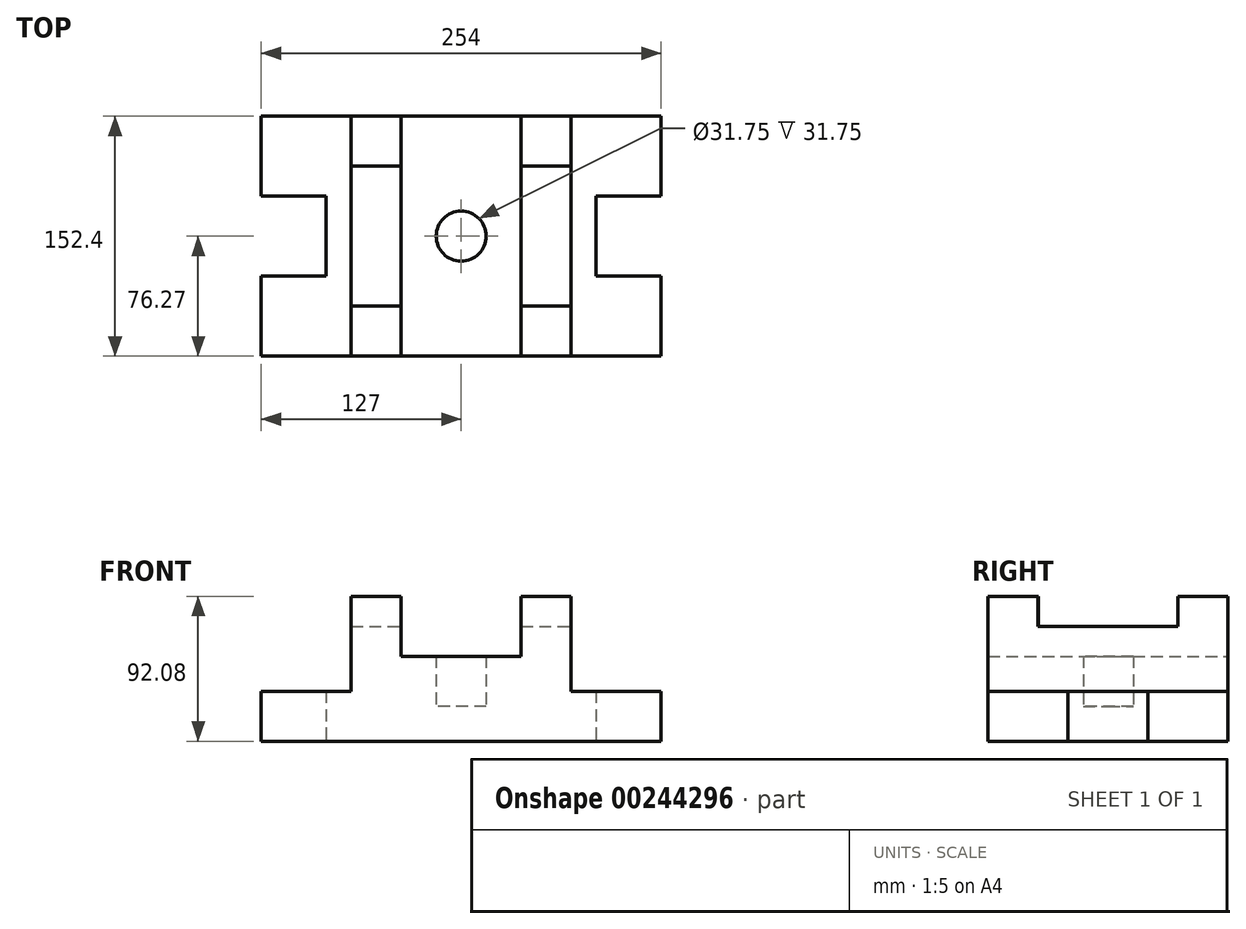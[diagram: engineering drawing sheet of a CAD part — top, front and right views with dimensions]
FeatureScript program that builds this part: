
annotation { "Feature Type Name" : "Feature", "Feature Type Description" : "" }
export const myFeature = defineFeature(function(context is Context, id is Id, definition is map)
    precondition{}
    {
        {
            var Q0;
            Q0=qCreatedBy(makeId("Top.planeOp"),FACE);
            var sketch = newSketch(context, id + "F0", { "sketchPlane" : qUnion([Q0])});
            skCircle(sketch, "E0", {"center": v(0, 0) * mm, "radius": 15.88 * mm});
            skLineSegment(sketch, "E1.bottom", {"start": v(-38.1, -76.27) * mm, "end": v(38.1, -76.27) * mm});
            skLineSegment(sketch, "E1.top", {"start": v(-38.1, 76.13) * mm, "end": v(38.1, 76.13) * mm});
            skLineSegment(sketch, "E1.left", {"start": v(-38.1, -76.27) * mm, "end": v(-38.1, 76.13) * mm});
            skLineSegment(sketch, "E1.right", {"start": v(38.1, -76.27) * mm, "end": v(38.1, 76.13) * mm});
            skLineSegment(sketch, "E2.bottom", {"start": v(38.1, 76.13) * mm, "end": v(69.85, 76.13) * mm});
            skLineSegment(sketch, "E2.top", {"start": v(38.1, 44.38) * mm, "end": v(69.85, 44.38) * mm});
            skLineSegment(sketch, "E2.left", {"start": v(38.1, 76.13) * mm, "end": v(38.1, 44.38) * mm});
            skLineSegment(sketch, "E2.right", {"start": v(69.85, 76.13) * mm, "end": v(69.85, 44.38) * mm});
            skLineSegment(sketch, "E3.bottom", {"start": v(38.1, -76.27) * mm, "end": v(69.85, -76.27) * mm});
            skLineSegment(sketch, "E3.top", {"start": v(38.1, -44.52) * mm, "end": v(69.85, -44.52) * mm});
            skLineSegment(sketch, "E3.left", {"start": v(38.1, -76.27) * mm, "end": v(38.1, -44.52) * mm});
            skLineSegment(sketch, "E3.right", {"start": v(69.85, -76.27) * mm, "end": v(69.85, -44.52) * mm});
            skLineSegment(sketch, "E4", {"start": v(69.85, 44.38) * mm, "end": v(69.85, -44.52) * mm});
            skLineSegment(sketch, "E5.MirrorCS", {"start": v(-38.1, -76.27) * mm, "end": v(-69.85, -76.27) * mm});
            skLineSegment(sketch, "E6.bottom", {"start": v(69.85, -76.27) * mm, "end": v(127, -76.27) * mm});
            skLineSegment(sketch, "E6.top", {"start": v(69.85, 76.13) * mm, "end": v(127, 76.13) * mm});
            skLineSegment(sketch, "E6.left", {"start": v(69.85, -76.27) * mm, "end": v(69.85, 76.13) * mm});
            skLineSegment(sketch, "E7.MirrorCS", {"start": v(-69.85, 76.13) * mm, "end": v(-127, 76.13) * mm});
            skLineSegment(sketch, "E8.MirrorCS", {"start": v(-127, -76.27) * mm, "end": v(-127, -25.47) * mm});
            skLineSegment(sketch, "E9.MirrorCS", {"start": v(-69.85, -76.27) * mm, "end": v(-127, -76.27) * mm});
            skLineSegment(sketch, "E10", {"start": v(127, -76.27) * mm, "end": v(127, -25.47) * mm});
            skLineSegment(sketch, "E11.bottom", {"start": v(127, 25.33) * mm, "end": v(85.73, 25.33) * mm});
            skLineSegment(sketch, "E11.top", {"start": v(127, -25.47) * mm, "end": v(85.73, -25.47) * mm});
            skLineSegment(sketch, "E11.right", {"start": v(85.73, 25.33) * mm, "end": v(85.73, -25.47) * mm});
            skLineSegment(sketch, "E12.trimOffspring", {"start": v(127, 25.33) * mm, "end": v(127, 76.13) * mm});
            skLineSegment(sketch, "E13.MirrorCS", {"start": v(-127, 25.33) * mm, "end": v(-85.73, 25.33) * mm});
            skLineSegment(sketch, "E14.MirrorCS", {"start": v(-85.73, 25.33) * mm, "end": v(-85.73, -25.47) * mm});
            skLineSegment(sketch, "E15.MirrorCS", {"start": v(-127, -25.47) * mm, "end": v(-85.73, -25.47) * mm});
            skLineSegment(sketch, "E16.trimOffspring", {"start": v(-127, 25.33) * mm, "end": v(-127, 76.13) * mm});
            skLineSegment(sketch, "E17.0", {"start": v(-38.21, 107.88) * mm, "end": v(-69.96, 107.88) * mm});
            skLineSegment(sketch, "E18", {"start": v(-69.85, 76.13) * mm, "end": v(-69.85, -76.27) * mm});
            skLineSegment(sketch, "E19.bottom", {"start": v(-69.85, 76.13) * mm, "end": v(-38.1, 76.13) * mm});
            skLineSegment(sketch, "E19.top", {"start": v(-69.85, 44.38) * mm, "end": v(-38.1, 44.38) * mm});
            skLineSegment(sketch, "E19.left", {"start": v(-69.85, 76.13) * mm, "end": v(-69.85, 44.38) * mm});
            skLineSegment(sketch, "E19.right", {"start": v(-38.1, 76.13) * mm, "end": v(-38.1, 44.38) * mm});
            skLineSegment(sketch, "E20.MirrorCS", {"start": v(-69.85, -44.38) * mm, "end": v(-38.1, -44.38) * mm});
            skSolve(sketch);
        }
        {
            var Q0;
            {var subQ0=sQuery(id+"F0.wireOp",EDGE,"E3.bottom");Q0=makeQuery(id+"F0.imprint","IMPRINT",FACE,{"disambiguationData":[TD([[makeQuery(id+"F0.imprint","IMPRINT",EDGE,{"derivedFrom":subQ0}),1.0]])]});}
            var Q1;
            {var subQ0=sQuery(id+"F0.wireOp",EDGE,"E2.bottom");Q1=makeQuery(id+"F0.imprint","IMPRINT",FACE,{"disambiguationData":[TD([[makeQuery(id+"F0.imprint","IMPRINT",EDGE,{"derivedFrom":subQ0}),-1.0]])]});}
            var Q2;
            Q2=makeQuery(id+"F0.imprint","IMPRINT",FACE,{"disambiguationData":[TD([[makeQuery(id+"F0.imprint","IMPRINT",EDGE,{"derivedFrom":sQuery(id+"F0.wireOp",EDGE,"E19.bottom")}),-1.0]])]});
            var Q3;
            {var subQ0=sQuery(id+"F0.wireOp",EDGE,"E5.MirrorCS");Q3=makeQuery(id+"F0.imprint","IMPRINT",FACE,{"disambiguationData":[TD([[makeQuery(id+"F0.imprint","IMPRINT",EDGE,{"derivedFrom":subQ0}),-1.0]])]});}
            extrude(context, id + "F1", {"entities" : qUnion([Q0, Q1, Q2, Q3]), "depth" : 92.07 * mm});
        }
        {
            var Q0;
            Q0=makeQuery(id+"F0.imprint","IMPRINT",FACE,{"disambiguationData":[TD([[makeQuery(id+"F0.imprint","IMPRINT",EDGE,{"derivedFrom":sQuery(id+"F0.wireOp",EDGE,"E7.MirrorCS")}),1.0]])]});
            var Q1;
            {var subQ3=sQuery(id+"F0.wireOp",EDGE,"E6.bottom");Q1=makeQuery(id+"F0.imprint","IMPRINT",FACE,{"disambiguationData":[TD([[makeQuery(id+"F0.imprint","IMPRINT",EDGE,{"derivedFrom":subQ3}),1.0]])]});}
            extrude(context, id + "F2", {"entities" : qUnion([Q0, Q1]), "operationType" : NewBodyOperationType.ADD, "depth" : 31.75 * mm});
        }
        {
            var Q0;
            {var subQ0=sQuery(id+"F0.wireOp",EDGE,"E19.top");Q0=makeQuery(id+"F0.imprint","IMPRINT",FACE,{"disambiguationData":[TD([[makeQuery(id+"F0.imprint","IMPRINT",EDGE,{"derivedFrom":subQ0}),-1.0]])]});}
            var Q1;
            Q1=makeQuery(id+"F0.imprint","IMPRINT",FACE,{"disambiguationData":[TD([[makeQuery(id+"F0.imprint","IMPRINT",EDGE,{"derivedFrom":sQuery(id+"F0.wireOp",EDGE,"E1.right")}),-1.0]])]});
            extrude(context, id + "F3", {"entities" : qUnion([Q0, Q1]), "operationType" : NewBodyOperationType.ADD, "depth" : 73.02 * mm});
        }
        {
            var Q0;
            Q0=makeQuery(id+"F0.imprint","IMPRINT",FACE,{"disambiguationData":[TD([[makeQuery(id+"F0.imprint","IMPRINT",EDGE,{"derivedFrom":sQuery(id+"F0.wireOp",EDGE,"E0")}),-1.0]])]});
            extrude(context, id + "F4", {"entities" : qUnion([Q0]), "operationType" : NewBodyOperationType.ADD, "depth" : 53.97 * mm});
        }
        {
            var Q0;
            Q0=makeQuery(id+"F0.imprint","IMPRINT",FACE,{"disambiguationData":[TD([[makeQuery(id+"F0.imprint","IMPRINT",EDGE,{"derivedFrom":sQuery(id+"F0.wireOp",EDGE,"E0")}),1.0]])]});
            extrude(context, id + "F5", {"entities" : qUnion([Q0]), "operationType" : NewBodyOperationType.ADD, "depth" : 22.22 * mm});
        }
    });
